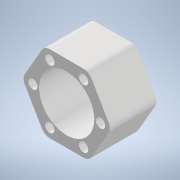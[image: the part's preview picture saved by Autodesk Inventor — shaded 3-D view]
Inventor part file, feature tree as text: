
AUTODESK INVENTOR PART (.ipt)
format: ipt  version: 2020 (Build 240168000, 168)  size: 152,064 bytes
history: native  units: in
note: dims shown in document units (in); Inventor stores cm internally (conversion verified against a paired STEP export)
features: other x2, extrude x1, fillet x1, sketch x1, reference x1
ambient origin geometry x8: Origin, YZ Plane, XZ Plane, XY Plane, X Axis, Y Axis, Z Axis, Center Point
bodies: Solid1 (feature_tree)
feature tree (6):
  extrude  "Extrusion1"  Depth=1.0in TaperAngle=0.0deg
  fillet  "Fillet1"  Radius=0.198in
  sketch  "Sketch1"  dims[d0=0.2in d3=1.0in d4=0.0in d5=0.198in d6=1.45in d7=0.2677in d8=0.3961in]
  reference  "Reference1"
  other  "Assembly1"
  other  "VersaFrame_End_Bearing_Gusset_217-3554:2"
